# Revit family: P810021-030-30
name_source: partatom
category: Lighting Fixtures
revit_build: Autodesk Revit 2014 (Build: 20130308_1515(x64)
units: mm (PartAtom-declared; Revit-internal decimal feet)

## types (1)
- P810021-030-30
    Apparent Load = 20 VA
    Assembly Code = D5020200
    Color Filter = 16777215
    Default Elevation = 48 "
    Description = Edgelit technology creates a large glare-free and evenly illuminated surface for a variety of applications for both residential and commercial settings. Offering a low-profile design, LED Flush Mount is available in three sizes: 7inch, 11inch, and 14inch, in a White finish. The integrated driver does not recess into junction box, allowing for easy installation into 4inch octagonal, 4inch round PVC and 4-1/2inch ceiling pan junction boxes. Wet location listed and offers a 50,000-hour LED life.
    Dimming Lamp Color Temperature Shift = <None>
    Emit Shape Visible in Rendering = No
    Emit from Rectangle Length = 12 "
    Emit from Rectangle Width = 12 "
    Features = •	14inch square Everlume Edgelit surface mount with LED technology 3000K, 90 CRI, 1600 lumens (delivered)
•	Simple installation to steel mounting plate
•	Fixture is adjustable after installation, allowing for easy alignment
•	Light weight non-conductive polycarbonate luminaire construction
•	Polycarbonate diffuser and acrylic light guide controls glare and provides an evenly illuminated surface
•	Integrated DC LED power supply capable of flicker-free dimming to 10% brightness with many Triac/Forward Phase and ELV/Reverse Phase dimmers
•	Can be installed to 4inch octagonal j-box, 4x1/2inch round shallow j-box and 4inch round PVC j-box
•	Can be mounted on ceiling or wall
•	Suitable for use in IC or Non-IC applications
•	Meets California Title 24 JA8-2019 and is Energy Star listed
•	Suitable for use in clothes closets when installed in accordance with the NEC 410.16 spacing requirements.
•	Maximum 25 luminaires on a circuit (without dimmer).
•	50,000 hour rated lifetime
    Fixture distribution = Direct
    Glass = Hubbell - White Glass
    Housing Material = Paint - Hubbell - White Texture
    Lamp = LED
    Load Classification = Lighting
    Manufacturer = Progress Lighting
    Model = P810021-030-30
    Photometric Web File = generic
    Power Factor = 1
    Product Documentation Link = https://hubbellcdn.com
    Product Link = https://www.hubbell.com
    Square = 14 "
    Tilt Angle = 60.00°
    URL = https://www.hubbell.com
    Voltage = 120 V
    Warranty = 1 year Warranty
    Wattage Comments = 20W
    Watts = 20 W

## geometry (parser evidence)
native form markers: Sweep x4
no freeform markers — native parametric forms only
